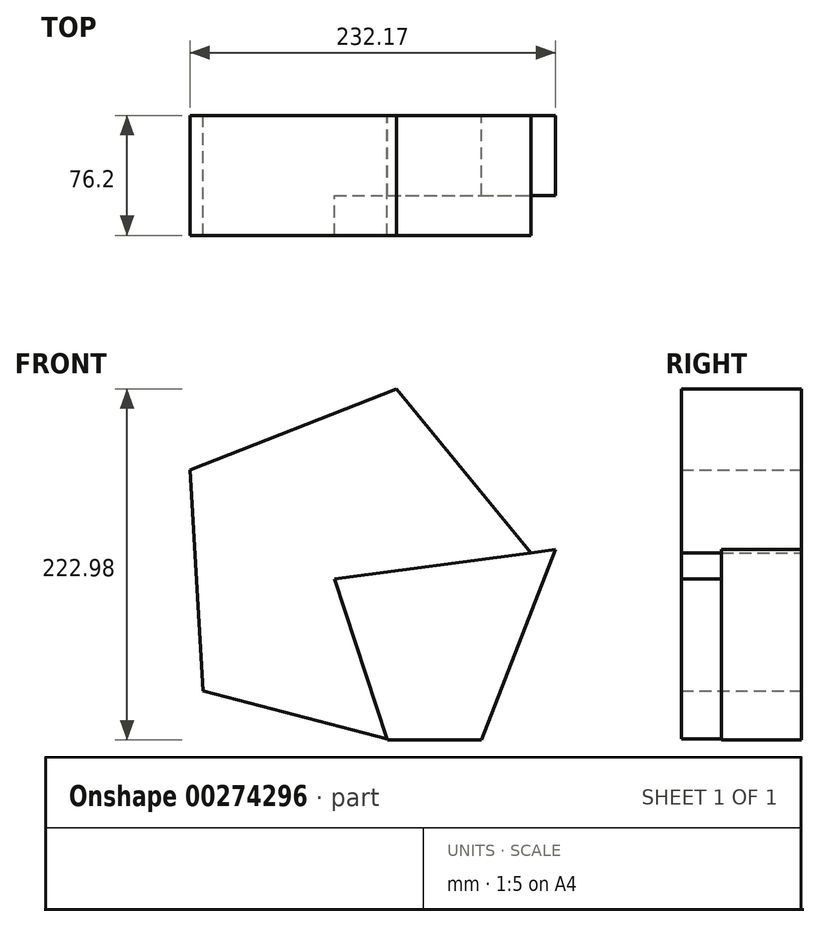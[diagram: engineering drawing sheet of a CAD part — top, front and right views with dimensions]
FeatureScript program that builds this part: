
annotation { "Feature Type Name" : "Feature", "Feature Type Description" : "" }
export const myFeature = defineFeature(function(context is Context, id is Id, definition is map)
    precondition{}
    {
        {
            var Q0;
            Q0=qCreatedBy(makeId("Front.planeOp"),FACE);
            var sketch = newSketch(context, id + "F0", { "sketchPlane" : qUnion([Q0])});
            skLineSegment(sketch, "E0", {"start": v(-67.24, 47.29) * mm, "end": v(-33.62, -54.9) * mm});
            skLineSegment(sketch, "E1", {"start": v(-33.62, -54.9) * mm, "end": v(26, -54.9) * mm});
            skLineSegment(sketch, "E2", {"start": v(26, -54.9) * mm, "end": v(73.06, 66.12) * mm});
            skLineSegment(sketch, "E3", {"start": v(-67.24, 47.29) * mm, "end": v(73.06, 66.12) * mm});
            skSolve(sketch);
        }
        {
            var Q0;
            Q0=makeQuery(id+"F0.imprint","IMPRINT",FACE,{"disambiguationData":[TD([[makeQuery(id+"F0.imprint","IMPRINT",EDGE,{"derivedFrom":sQuery(id+"F0.wireOp",EDGE,"E0")}),1.0]])]});
            var sketch = newSketch(context, id + "F1", { "sketchPlane" : qUnion([Q0])});
            skCircle(sketch, "E4.cCircle", {"center": v(-58.27, 52.22) * mm, "radius": 96.86 * mm, "construction": true});
            skLineSegment(sketch, "E4.0", {"start": v(61.25, 59.27) * mm, "end": v(-14.63, -59.27) * mm});
            skLineSegment(sketch, "E4.1", {"start": v(-14.63, -59.27) * mm, "end": v(-150.82, -23.74) * mm});
            skLineSegment(sketch, "E4.2", {"start": v(-150.82, -23.74) * mm, "end": v(-159.1, 116.77) * mm});
            skLineSegment(sketch, "E4.3", {"start": v(-159.1, 116.77) * mm, "end": v(-28.04, 168.07) * mm});
            skLineSegment(sketch, "E4.4", {"start": v(-28.04, 168.07) * mm, "end": v(61.25, 59.27) * mm});
            skPoint(sketch, "E4.0.midPoint", {"position": v(23.3, 0) * mm});
            skSolve(sketch);
        }
        {
            var Q0;
            {var subQ4=sQuery(id+"F1.wireOp",EDGE,"E4.2");Q0=makeQuery(id+"F1.imprint","IMPRINT",FACE,{"disambiguationData":[TD([[makeQuery(id+"F1.imprint","IMPRINT",EDGE,{"derivedFrom":subQ4}),-1.0]])]});}
            extrude(context, id + "F2", {"entities" : qUnion([Q0]), "depth" : 76.2 * mm});
        }
        {
            var Q0;
            Q0=makeQuery(id+"F0.imprint","IMPRINT",FACE,{"disambiguationData":[TD([[makeQuery(id+"F0.imprint","IMPRINT",EDGE,{"derivedFrom":sQuery(id+"F0.wireOp",EDGE,"E0")}),1.0]])]});
            extrude(context, id + "F3", {"entities" : qUnion([Q0]), "operationType" : NewBodyOperationType.ADD, "depth" : 50.8 * mm});
        }
    });
